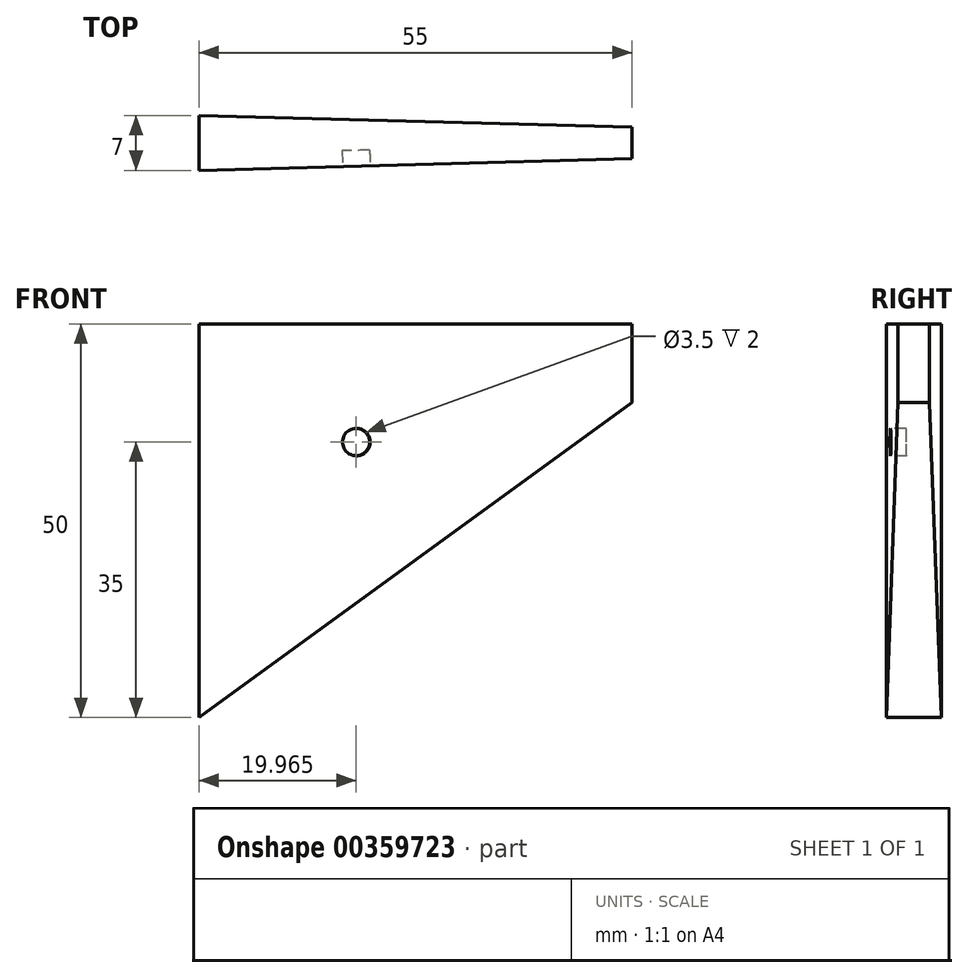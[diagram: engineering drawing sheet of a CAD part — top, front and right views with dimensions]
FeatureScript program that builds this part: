
annotation { "Feature Type Name" : "Feature", "Feature Type Description" : "" }
export const myFeature = defineFeature(function(context is Context, id is Id, definition is map)
    precondition{}
    {
        {
            var Q0;
            Q0=qCreatedBy(makeId("Front.planeOp"),FACE);
            var sketch = newSketch(context, id + "F0", { "sketchPlane" : qUnion([Q0])});
            skLineSegment(sketch, "E0.bottom", {"start": v(27.5, 25) * mm, "end": v(-27.5, 25) * mm});
            skLineSegment(sketch, "E0.top", {"start": v(27.5, -25) * mm, "end": v(-27.5, -25) * mm});
            skLineSegment(sketch, "E0.left", {"start": v(27.5, 25) * mm, "end": v(27.5, -25) * mm});
            skLineSegment(sketch, "E0.right", {"start": v(-27.5, 25) * mm, "end": v(-27.5, -25) * mm});
            skPoint(sketch, "E0.middle", {"position": v(0, 0) * mm});
            skLineSegment(sketch, "E1", {"start": v(-27.5, -25) * mm, "end": v(27.5, 15) * mm});
            skSolve(sketch);
        }
        {
            var Q0;
            {var subQ0=sQuery(id+"F0.wireOp",EDGE,"E0.bottom");Q0=makeQuery(id+"F0.imprint","IMPRINT",FACE,{"disambiguationData":[TD([[makeQuery(id+"F0.imprint","IMPRINT",EDGE,{"derivedFrom":subQ0}),1.0]])]});}
            extrude(context, id + "F1", {"entities" : qUnion([Q0]), "depth" : 7 * mm});
        }
        {
            var Q0;
            Q0=makeQuery(id+"F1.opExtrude","SWEPT_FACE",FACE,{"disambiguationData":[OSD([sQuery(id+"F0.wireOp",EDGE,"E0.bottom")])]});
            var sketch = newSketch(context, id + "F2", { "sketchPlane" : qUnion([Q0])});
            skLineSegment(sketch, "E2", {"start": v(-27.5, 0) * mm, "end": v(27.5, -1.5) * mm});
            skLineSegment(sketch, "E3", {"start": v(-27.5, -7) * mm, "end": v(27.5, -5.5) * mm});
            skSolve(sketch);
        }
        {
            var Q0;
            {var subQ0=sQuery(id+"F2.wireOp",EDGE,"E2");Q0=makeQuery(id+"F2.imprint","IMPRINT",FACE,{"disambiguationData":[TD([[makeQuery(id+"F2.imprint","IMPRINT",EDGE,{"derivedFrom":subQ0}),1.0]])]});}
            var Q1;
            {var subQ0=sQuery(id+"F2.wireOp",EDGE,"E3");Q1=makeQuery(id+"F2.imprint","IMPRINT",FACE,{"disambiguationData":[TD([[makeQuery(id+"F2.imprint","IMPRINT",EDGE,{"derivedFrom":subQ0}),-1.0]])]});}
            extrude(context, id + "F3", {"entities" : qUnion([Q0, Q1]), "operationType" : NewBodyOperationType.REMOVE, "endBound" : BoundingType.THROUGH_ALL, "oppositeDirection" : true, "depth" : 25 * mm});
        }
        {
            var Q0;
            Q0=makeQuery(id+"F3.boolean.opBoolean","COPY",FACE,{"derivedFrom":makeQuery(id+"F3.opExtrude","SWEPT_FACE",FACE,{"disambiguationData":[OSD([sQuery(id+"F2.wireOp",EDGE,"E3")])]})});
            var sketch = newSketch(context, id + "F4", { "sketchPlane" : qUnion([Q0])});
            skCircle(sketch, "E4", {"center": v(-7.68, 10) * mm, "radius": 1.75 * mm});
            skSolve(sketch);
        }
        {
            var Q0;
            Q0=makeQuery(id+"F4.imprint","IMPRINT",FACE,{"disambiguationData":[TD([[makeQuery(id+"F4.imprint","IMPRINT",EDGE,{"derivedFrom":sQuery(id+"F4.wireOp",EDGE,"E4")}),1.0]])]});
            extrude(context, id + "F5", {"entities" : qUnion([Q0]), "operationType" : NewBodyOperationType.REMOVE, "oppositeDirection" : true, "depth" : 2 * mm});
        }
    });
